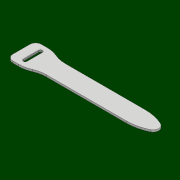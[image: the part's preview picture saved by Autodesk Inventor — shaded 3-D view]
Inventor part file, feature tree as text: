
AUTODESK INVENTOR PART (.ipt)
format: ipt  version: 2018 (Build 220112000, 112)  size: 109,568 bytes
history: native  units: mm
features: other x1, extrude x1, fillet x1, sketch x1
ambient origin geometry x8: Origin, YZ Plane, XZ Plane, XY Plane, X Axis, Y Axis, Z Axis, Center Point
bodies: Body1 (feature_tree)
feature tree (4):
  other  "ソリッド1"
  extrude  "押し出し1"  Depth=2.0mm
  fillet  "フィレット1"  Radius=10.0mm
  sketch  "スケッチ1"
